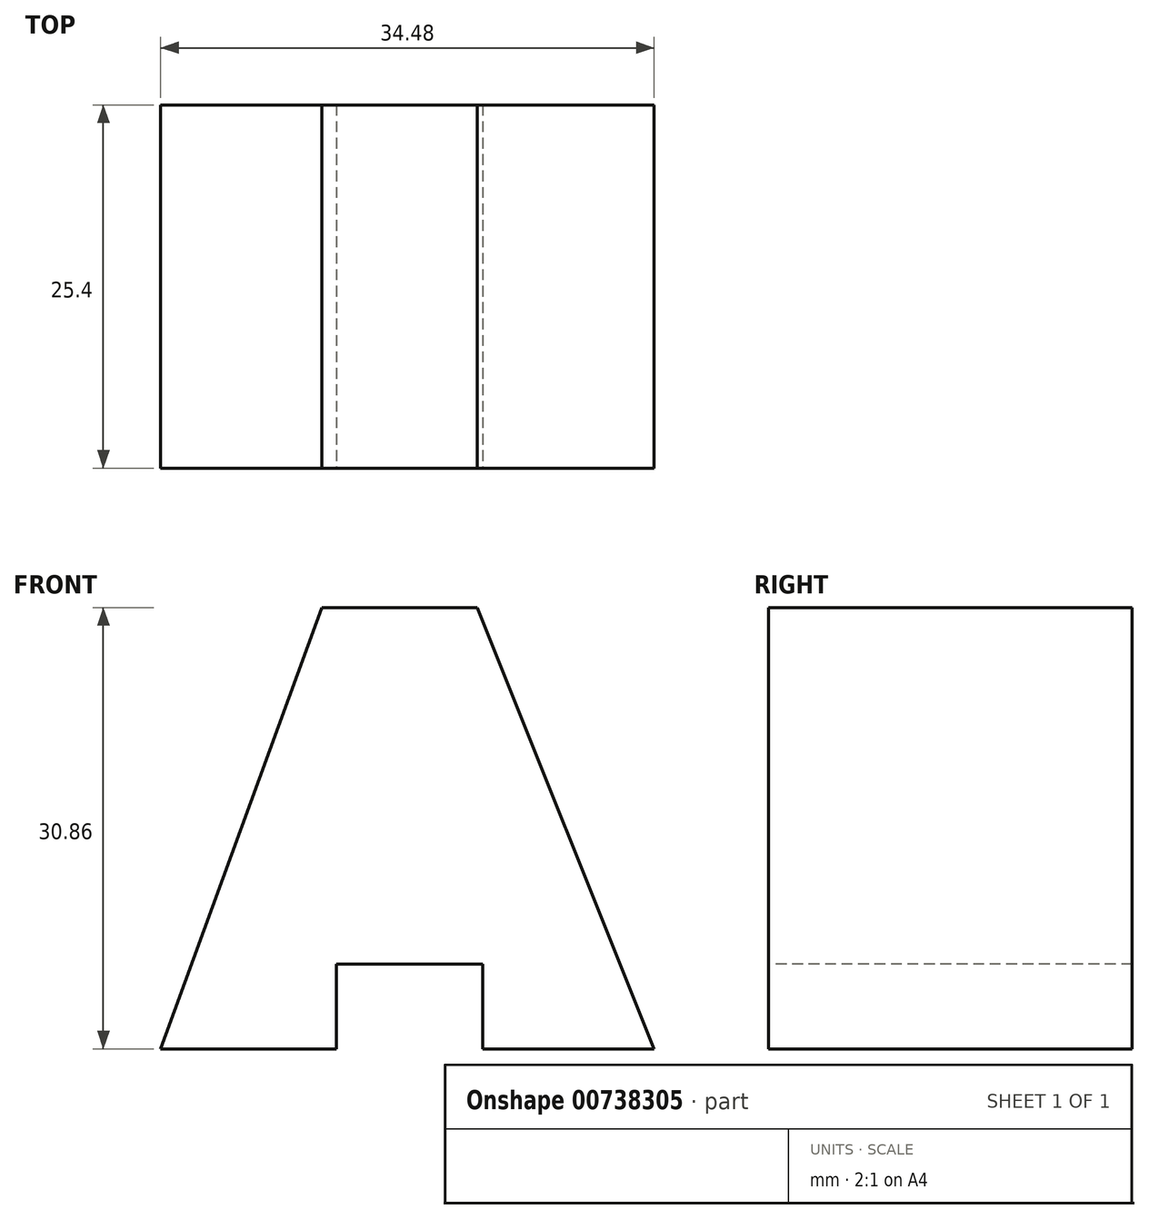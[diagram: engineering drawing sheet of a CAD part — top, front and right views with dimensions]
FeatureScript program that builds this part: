
annotation { "Feature Type Name" : "Feature", "Feature Type Description" : "" }
export const myFeature = defineFeature(function(context is Context, id is Id, definition is map)
    precondition{}
    {
        {
            var Q0;
            Q0=qCreatedBy(makeId("Front.planeOp"),FACE);
            var sketch = newSketch(context, id + "F0", { "sketchPlane" : qUnion([Q0])});
            skLineSegment(sketch, "E0", {"start": v(0, 0) * mm, "end": v(0, 30.86) * mm});
            skLineSegment(sketch, "E1", {"start": v(0, 30.86) * mm, "end": v(34.48, 30.86) * mm});
            skLineSegment(sketch, "E2", {"start": v(34.48, 30.86) * mm, "end": v(34.48, 0) * mm});
            skLineSegment(sketch, "E3", {"start": v(34.48, 0) * mm, "end": v(0, 0) * mm});
            skSolve(sketch);
        }
        {
            var Q0;
            Q0=makeQuery(id+"F0.imprint","IMPRINT",FACE,{"disambiguationData":[TD([[makeQuery(id+"F0.imprint","IMPRINT",EDGE,{"derivedFrom":sQuery(id+"F0.wireOp",EDGE,"E0")}),-1.0]])]});
            extrude(context, id + "F1", {"entities" : qUnion([Q0]), "depth" : 25.4 * mm, "offsetDistance" : 25.4 * mm});
        }
        {
            var Q0;
            Q0=makeQuery(id+"F1.opExtrude","CAP_FACE",FACE,{"disambiguationData":[OSD([sQuery(id+"F0.wireOp",EDGE,"E0"),sQuery(id+"F0.wireOp",EDGE,"E1"),sQuery(id+"F0.wireOp",EDGE,"E2"),sQuery(id+"F0.wireOp",EDGE,"E3")])],"isStart":false});
            var sketch = newSketch(context, id + "F2", { "sketchPlane" : qUnion([Q0])});
            skLineSegment(sketch, "E4", {"start": v(22.11, 30.86) * mm, "end": v(34.48, 0) * mm});
            skSolve(sketch);
        }
        {
            var Q0;
            {var subQ0=sQuery(id+"F2.wireOp",EDGE,"E4");Q0=makeQuery(id+"F2.imprint","IMPRINT",FACE,{"disambiguationData":[TD([[makeQuery(id+"F2.imprint","IMPRINT",EDGE,{"derivedFrom":subQ0}),-1.0]])]});}
            var sketch = newSketch(context, id + "F3", { "sketchPlane" : qUnion([Q0])});
            skLineSegment(sketch, "E5", {"start": v(0, 0) * mm, "end": v(11.26, 30.86) * mm});
            skLineSegment(sketch, "E6", {"start": v(11.26, 30.86) * mm, "end": v(22.11, 30.86) * mm});
            skSolve(sketch);
        }
        {
            var Q0;
            {var subQ0=sQuery(id+"F2.wireOp",EDGE,"E4");Q0=makeQuery(id+"F2.imprint","IMPRINT",FACE,{"disambiguationData":[TD([[makeQuery(id+"F2.imprint","IMPRINT",EDGE,{"derivedFrom":subQ0}),1.0]])]});}
            extrude(context, id + "F4", {"entities" : qUnion([Q0]), "operationType" : NewBodyOperationType.REMOVE, "oppositeDirection" : true, "depth" : 25.4 * mm, "offsetDistance" : 25.4 * mm});
        }
        {
            var Q0;
            {var subQ0=sQuery(id+"F3.wireOp",EDGE,"E5");Q0=makeQuery(id+"F3.imprint","IMPRINT",FACE,{"disambiguationData":[TD([[makeQuery(id+"F3.imprint","IMPRINT",EDGE,{"derivedFrom":subQ0}),1.0]])]});}
            extrude(context, id + "F5", {"entities" : qUnion([Q0]), "operationType" : NewBodyOperationType.REMOVE, "oppositeDirection" : true, "depth" : 25.4 * mm, "offsetDistance" : 25.4 * mm});
        }
        {
            var Q0;
            Q0=makeQuery(id+"F1.opExtrude","CAP_FACE",FACE,{"disambiguationData":[OSD([sQuery(id+"F0.wireOp",EDGE,"E0"),sQuery(id+"F0.wireOp",EDGE,"E1"),sQuery(id+"F0.wireOp",EDGE,"E2"),sQuery(id+"F0.wireOp",EDGE,"E3")])],"isStart":false});
            var sketch = newSketch(context, id + "F6", { "sketchPlane" : qUnion([Q0])});
            skLineSegment(sketch, "E7", {"start": v(22.52, 0) * mm, "end": v(22.52, 5.93) * mm});
            skLineSegment(sketch, "E8", {"start": v(22.52, 5.93) * mm, "end": v(12.26, 5.93) * mm});
            skLineSegment(sketch, "E9", {"start": v(12.26, 5.93) * mm, "end": v(12.26, 0) * mm});
            skLineSegment(sketch, "E10", {"start": v(12.26, 0) * mm, "end": v(22.52, 0) * mm});
            skSolve(sketch);
        }
        {
            var Q0;
            Q0=makeQuery(id+"F6.imprint","IMPRINT",FACE,{"disambiguationData":[TD([[makeQuery(id+"F6.imprint","IMPRINT",EDGE,{"derivedFrom":sQuery(id+"F6.wireOp",EDGE,"E7")}),1.0]])]});
            extrude(context, id + "F7", {"entities" : qUnion([Q0]), "operationType" : NewBodyOperationType.REMOVE, "oppositeDirection" : true, "depth" : 25.4 * mm, "offsetDistance" : 25.4 * mm});
        }
    });
